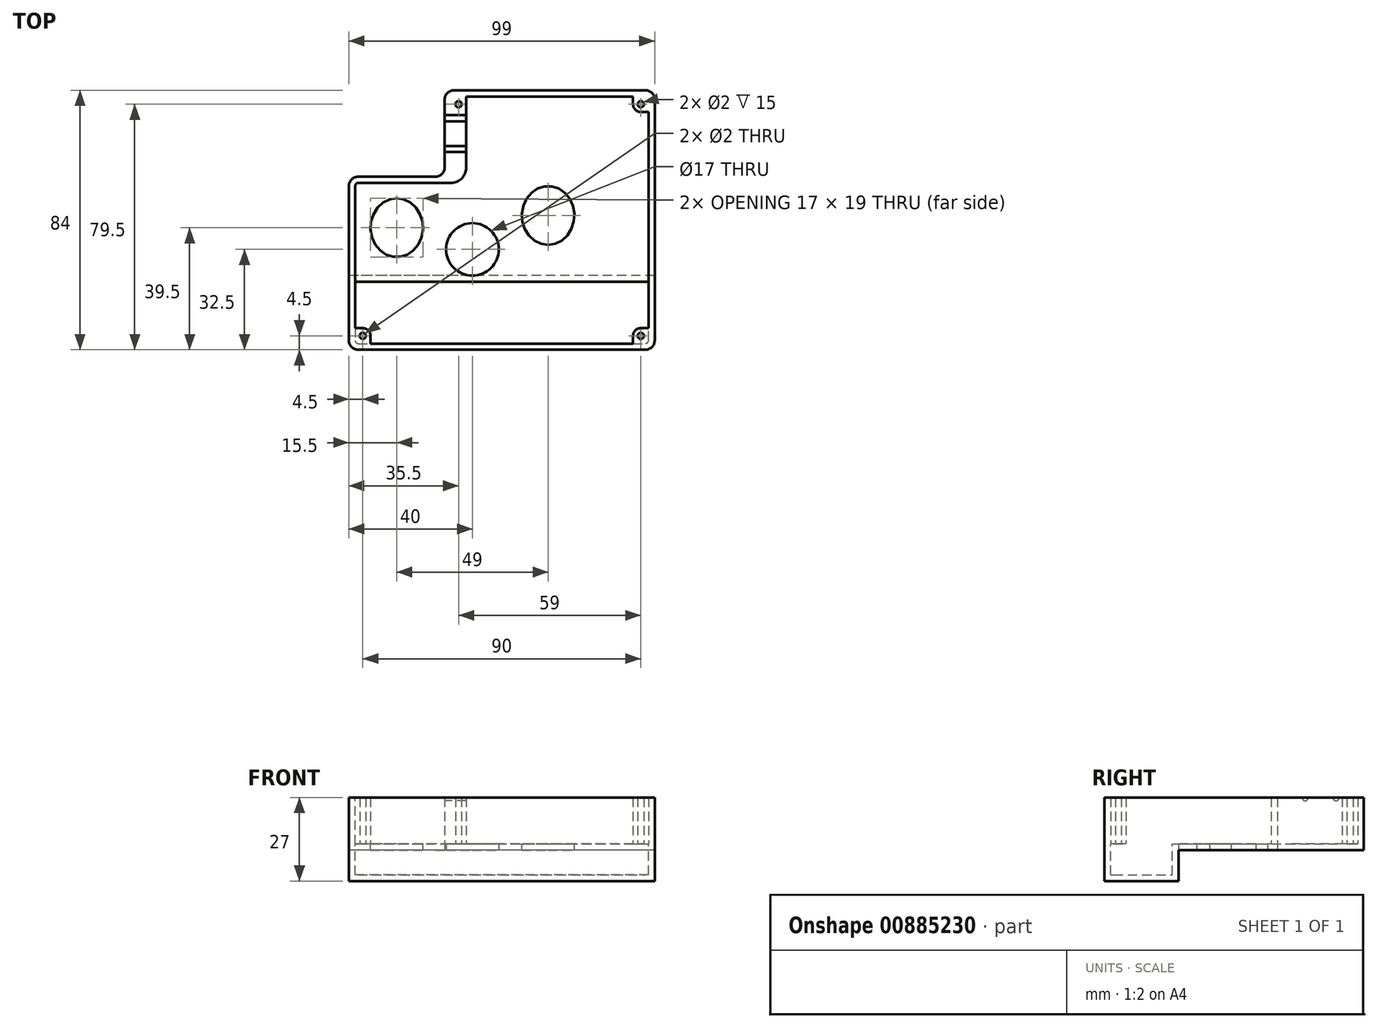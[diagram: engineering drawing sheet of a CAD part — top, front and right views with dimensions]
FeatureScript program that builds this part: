
annotation { "Feature Type Name" : "Feature", "Feature Type Description" : "" }
export const myFeature = defineFeature(function(context is Context, id is Id, definition is map)
    precondition{}
    {
        {
            var Q0;
            Q0=qCreatedBy(makeId("Top.planeOp"),FACE);
            var sketch = newSketch(context, id + "F0", { "sketchPlane" : qUnion([Q0])});
            skPoint(sketch, "E0.middle", {"position": v(0, 0) * mm});
            skPoint(sketch, "E1.visualSharp", {"position": v(-40.5, 17.5) * mm});
            skArc(sketch, "E1.filletArc", {"start": v(-37.5, 17.5) * mm, "mid": v(-39.62, 16.62) * mm, "end": v(-40.5, 14.5) * mm});
            skPoint(sketch, "E2.visualSharp", {"position": v(40.5, 17.5) * mm});
            skLineSegment(sketch, "E3", {"start": v(40.5, 17.5) * mm, "end": v(40.5, 42.5) * mm});
            skLineSegment(sketch, "E4", {"start": v(37.5, 45.5) * mm, "end": v(-6.5, 45.5) * mm});
            skLineSegment(sketch, "E5", {"start": v(-9.5, 42.5) * mm, "end": v(-9.5, 20.5) * mm});
            skLineSegment(sketch, "E6", {"start": v(-12.5, 17.5) * mm, "end": v(-37.5, 17.5) * mm});
            skPoint(sketch, "E7.visualSharp", {"position": v(-9.5, 17.5) * mm});
            skArc(sketch, "E7.filletArc", {"start": v(-12.5, 17.5) * mm, "mid": v(-10.38, 18.38) * mm, "end": v(-9.5, 20.5) * mm});
            skPoint(sketch, "E8.visualSharp", {"position": v(-9.5, 45.5) * mm});
            skArc(sketch, "E8.filletArc", {"start": v(-6.5, 45.5) * mm, "mid": v(-8.62, 44.62) * mm, "end": v(-9.5, 42.5) * mm});
            skPoint(sketch, "E9.visualSharp", {"position": v(40.5, 45.5) * mm});
            skArc(sketch, "E9.filletArc", {"start": v(40.5, 42.5) * mm, "mid": v(39.62, 44.62) * mm, "end": v(37.5, 45.5) * mm});
            skLineSegment(sketch, "E10", {"start": v(40.5, 17.5) * mm, "end": v(40.5, -17.5) * mm});
            skLineSegment(sketch, "E11", {"start": v(-40.5, -17.5) * mm, "end": v(-40.5, 14.5) * mm});
            skLineSegment(sketch, "E12", {"start": v(-40.5, -17.5) * mm, "end": v(-40.5, -17.5) * mm});
            skLineSegment(sketch, "E13", {"start": v(-40.5, -17.5) * mm, "end": v(-40.5, -35.5) * mm});
            skLineSegment(sketch, "E14", {"start": v(-37.5, -38.5) * mm, "end": v(55.5, -38.5) * mm});
            skLineSegment(sketch, "E15", {"start": v(58.5, -35.5) * mm, "end": v(58.5, -17.5) * mm});
            skLineSegment(sketch, "E16", {"start": v(58.5, -17.5) * mm, "end": v(40.5, -17.5) * mm});
            skLineSegment(sketch, "E17", {"start": v(58.5, -17.5) * mm, "end": v(58.5, 42.5) * mm});
            skLineSegment(sketch, "E18", {"start": v(55.5, 45.5) * mm, "end": v(37.5, 45.5) * mm});
            skPoint(sketch, "E19.visualSharp", {"position": v(58.5, -38.5) * mm});
            skArc(sketch, "E19.filletArc", {"start": v(55.5, -38.5) * mm, "mid": v(57.62, -37.62) * mm, "end": v(58.5, -35.5) * mm});
            skPoint(sketch, "E20.visualSharp", {"position": v(-40.5, -38.5) * mm});
            skArc(sketch, "E20.filletArc", {"start": v(-40.5, -35.5) * mm, "mid": v(-39.62, -37.62) * mm, "end": v(-37.5, -38.5) * mm});
            skPoint(sketch, "E21.visualSharp", {"position": v(58.5, 45.5) * mm});
            skArc(sketch, "E21.filletArc", {"start": v(58.5, 42.5) * mm, "mid": v(57.62, 44.62) * mm, "end": v(55.5, 45.5) * mm});
            skSolve(sketch);
        }
        {
            var Q0;
            Q0 = qSketchRegion(id + "F0", true);
            extrude(context, id + "F1", {"entities" : qUnion([Q0]), "depth" : 17 * mm, "offsetDistance" : 25 * mm});
        }
        {
            var Q0;
            Q0=qCreatedBy(makeId("Top.planeOp"),FACE);
            var sketch = newSketch(context, id + "F2", { "sketchPlane" : qUnion([Q0])});
            skEllipse(sketch, "E22", {"center": v(-25, 1) * mm, "majorRadius": 9.5 * mm, "minorRadius": 8.5 * mm, "majorAxis": v(0, 1)});
            skEllipse(sketch, "E23.MirrorC", {"center": v(24, 5) * mm, "majorRadius": 9.5 * mm, "minorRadius": 8.5 * mm, "majorAxis": v(0, -1)});
            skCircle(sketch, "E24", {"center": v(-0.5, -6) * mm, "radius": 8.5 * mm});
            skSolve(sketch);
        }
        {
            var Q0;
            Q0=makeQuery(id+"F1.opExtrude","CAP_FACE",FACE,{"disambiguationData":[OSD([sQuery(id+"F0.wireOp",EDGE,"E0.bottom"),sQuery(id+"F0.wireOp",EDGE,"E0.top"),sQuery(id+"F0.wireOp",EDGE,"E0.left"),sQuery(id+"F0.wireOp",EDGE,"E0.right"),sQuery(id+"F0.wireOp",EDGE,"E1.filletArc"),sQuery(id+"F0.wireOp",EDGE,"E2.filletArc"),sQuery(id+"F0.wireOp",EDGE,"fd3a0fd0-5bb6-43b4-b1ca-f7e2fdb911ee.filletArc"),sQuery(id+"F0.wireOp",EDGE,"6f945ab3-a14b-4210-82b2-7dc400fba289.filletArc"),sQuery(id+"F0.wireOp",EDGE,"lKBWg51h-oEnW-cZ2k-sGJy-vkzMBgg1EJc2")])],"isStart":false});
            shell(context, id + "F3", {"entities" : qUnion([Q0]), "thickness" : 2 * mm});
        }
        {
            var Q0;
            Q0 = qSketchRegion(id + "F2", true);
            extrude(context, id + "F4", {"entities" : qUnion([Q0]), "operationType" : NewBodyOperationType.REMOVE, "endBound" : BoundingType.UP_TO_NEXT, "depth" : 25 * mm, "offsetDistance" : 25 * mm});
        }
        {
            var Q0;
            Q0=makeQuery(id+"F3.opShell","OFFSET_FACE",FACE,{"disambiguationData":[OSD([sQuery(id+"F0.wireOp",EDGE,"E1.filletArc"),sQuery(id+"F0.wireOp",EDGE,"E4"),sQuery(id+"F0.wireOp",EDGE,"E5"),sQuery(id+"F0.wireOp",EDGE,"E6"),sQuery(id+"F0.wireOp",EDGE,"E7.filletArc"),sQuery(id+"F0.wireOp",EDGE,"E8.filletArc"),sQuery(id+"F0.wireOp",EDGE,"E11"),sQuery(id+"F0.wireOp",EDGE,"E13"),sQuery(id+"F0.wireOp",EDGE,"E14"),sQuery(id+"F0.wireOp",EDGE,"E15"),sQuery(id+"F0.wireOp",EDGE,"E17"),sQuery(id+"F0.wireOp",EDGE,"E18"),sQuery(id+"F0.wireOp",EDGE,"E19.filletArc"),sQuery(id+"F0.wireOp",EDGE,"E20.filletArc"),sQuery(id+"F0.wireOp",EDGE,"E21.filletArc")])]});
            var sketch = newSketch(context, id + "F5", { "sketchPlane" : qUnion([Q0])});
            skCircle(sketch, "E25.0", {"center": v(54, 41) * mm, "radius": 1 * mm});
            skLineSegment(sketch, "E26", {"start": v(54, 38.5) * mm, "end": v(56.5, 38.5) * mm});
            skLineSegment(sketch, "E27", {"start": v(51.5, 41) * mm, "end": v(51.5, 43.5) * mm});
            skArc(sketch, "E28", {"start": v(51.5, 41) * mm, "mid": v(52.23, 39.23) * mm, "end": v(54, 38.5) * mm});
            skLineSegment(sketch, "E29", {"start": v(56.5, 38.5) * mm, "end": v(56.5, 43.5) * mm});
            skLineSegment(sketch, "E30", {"start": v(56.5, 43.5) * mm, "end": v(51.5, 43.5) * mm});
            skLineSegment(sketch, "E31", {"start": v(24.5, 43.5) * mm, "end": v(24.5, 26.84) * mm, "construction": true});
            skLineSegment(sketch, "E32.MirrorCS", {"start": v(-7.5, 43.5) * mm, "end": v(-2.5, 43.5) * mm});
            skLineSegment(sketch, "E33.MirrorCS", {"start": v(-7.5, 38.5) * mm, "end": v(-7.5, 43.5) * mm});
            skCircle(sketch, "E34.MirrorC", {"center": v(-5, 41) * mm, "radius": 1 * mm});
            skLineSegment(sketch, "E35", {"start": v(56.5, 3.5) * mm, "end": v(42, 3.5) * mm, "construction": true});
            skLineSegment(sketch, "E36.MirrorCS", {"start": v(54, -31.5) * mm, "end": v(56.5, -31.5) * mm});
            skArc(sketch, "E37.MirrorCS", {"start": v(51.5, -34) * mm, "mid": v(52.23, -32.23) * mm, "end": v(54, -31.5) * mm});
            skLineSegment(sketch, "E38.MirrorCS", {"start": v(51.5, -34) * mm, "end": v(51.5, -36.5) * mm});
            skLineSegment(sketch, "E39.MirrorCS", {"start": v(56.5, -31.5) * mm, "end": v(56.5, -36.5) * mm});
            skLineSegment(sketch, "E40.MirrorCS", {"start": v(56.5, -36.5) * mm, "end": v(51.5, -36.5) * mm});
            skCircle(sketch, "E41.MirrorC", {"center": v(54, -34) * mm, "radius": 1 * mm});
            skLineSegment(sketch, "E42", {"start": v(9, -36.5) * mm, "end": v(9, -20.27) * mm, "construction": true});
            skLineSegment(sketch, "E43.MirrorCS", {"start": v(-33.5, -34) * mm, "end": v(-33.5, -36.5) * mm});
            skArc(sketch, "E44.MirrorCS", {"start": v(-33.5, -34) * mm, "mid": v(-34.23, -32.23) * mm, "end": v(-36, -31.5) * mm});
            skLineSegment(sketch, "E45.MirrorCS", {"start": v(-36, -31.5) * mm, "end": v(-38.5, -31.5) * mm});
            skCircle(sketch, "E46.MirrorC", {"center": v(-36, -34) * mm, "radius": 1 * mm});
            skLineSegment(sketch, "E47.MirrorCS", {"start": v(-38.5, -36.5) * mm, "end": v(-33.5, -36.5) * mm});
            skLineSegment(sketch, "E48.MirrorCS", {"start": v(-38.5, -31.5) * mm, "end": v(-38.5, -36.5) * mm});
            skLineSegment(sketch, "E49", {"start": v(-2.5, 43.5) * mm, "end": v(-2.5, 20.5) * mm});
            skLineSegment(sketch, "E50", {"start": v(-7.5, 15.5) * mm, "end": v(-12.5, 15.5) * mm});
            skLineSegment(sketch, "E51", {"start": v(-12.5, 15.5) * mm, "end": v(-7.5, 20.5) * mm});
            skLineSegment(sketch, "E52", {"start": v(-7.5, 20.5) * mm, "end": v(-7.5, 38.5) * mm});
            skPoint(sketch, "E53.visualSharp", {"position": v(-2.5, 15.5) * mm});
            skArc(sketch, "E53.filletArc", {"start": v(-7.5, 15.5) * mm, "mid": v(-3.96, 16.96) * mm, "end": v(-2.5, 20.5) * mm});
            skSolve(sketch);
        }
        {
            var Q0;
            Q0 = qSketchRegion(id + "F5", true);
            var Q1;
            {var subQ0=sQuery(id+"F0.wireOp",EDGE,"E19.filletArc");var subQ1=sQuery(id+"F0.wireOp",EDGE,"E17");var subQ2=sQuery(id+"F0.wireOp",EDGE,"E15");var subQ3=sQuery(id+"F0.wireOp",EDGE,"E21.filletArc");var subQ4=sQuery(id+"F0.wireOp",EDGE,"E14");var subQ5=sQuery(id+"F0.wireOp",EDGE,"E20.filletArc");var subQ6=sQuery(id+"F0.wireOp",EDGE,"E1.filletArc");var subQ7=sQuery(id+"F0.wireOp",EDGE,"E5");var subQ8=sQuery(id+"F0.wireOp",EDGE,"E18");var subQ9=sQuery(id+"F0.wireOp",EDGE,"E4");var subQ10=sQuery(id+"F0.wireOp",EDGE,"E6");var subQ11=sQuery(id+"F0.wireOp",EDGE,"E13");var subQ12=sQuery(id+"F0.wireOp",EDGE,"E11");var subQ13=sQuery(id+"F0.wireOp",EDGE,"E7.filletArc");var subQ14=sQuery(id+"F0.wireOp",EDGE,"E8.filletArc");Q1=makeQuery(id+"F8.boolean.opBoolean","SPLIT",FACE,{"disambiguationData":[TD([makeQuery(id+"F1.opExtrude","SWEPT_FACE",FACE,{"disambiguationData":[OSD([subQ6])]}),makeQuery(id+"F1.opExtrude","SWEPT_FACE",FACE,{"disambiguationData":[OSD([subQ9,subQ8])]}),makeQuery(id+"F1.opExtrude","SWEPT_FACE",FACE,{"disambiguationData":[OSD([subQ7])]}),makeQuery(id+"F1.opExtrude","SWEPT_FACE",FACE,{"disambiguationData":[OSD([subQ10])]}),makeQuery(id+"F1.opExtrude","SWEPT_FACE",FACE,{"disambiguationData":[OSD([subQ13])]}),makeQuery(id+"F1.opExtrude","SWEPT_FACE",FACE,{"disambiguationData":[OSD([subQ14])]}),makeQuery(id+"F1.opExtrude","SWEPT_FACE",FACE,{"disambiguationData":[OSD([subQ12,subQ11])]}),makeQuery(id+"F1.opExtrude","SWEPT_FACE",FACE,{"disambiguationData":[OSD([subQ4])]}),makeQuery(id+"F1.opExtrude","SWEPT_FACE",FACE,{"disambiguationData":[OSD([subQ2,subQ1])]}),makeQuery(id+"F1.opExtrude","SWEPT_FACE",FACE,{"disambiguationData":[OSD([subQ0])]}),makeQuery(id+"F1.opExtrude","SWEPT_FACE",FACE,{"disambiguationData":[OSD([subQ5])]}),makeQuery(id+"F1.opExtrude","SWEPT_FACE",FACE,{"disambiguationData":[OSD([subQ3])]}),makeQuery(id+"F3.opShell","OFFSET_FACE",FACE,{"disambiguationData":[OSD([subQ6])]}),makeQuery(id+"F3.opShell","OFFSET_FACE",FACE,{"disambiguationData":[OSD([subQ9,subQ8])]}),makeQuery(id+"F3.opShell","OFFSET_FACE",FACE,{"disambiguationData":[OSD([subQ7])]}),makeQuery(id+"F3.opShell","OFFSET_FACE",FACE,{"disambiguationData":[OSD([subQ10])]}),makeQuery(id+"F3.opShell","OFFSET_FACE",FACE,{"disambiguationData":[OSD([subQ13])]}),makeQuery(id+"F3.opShell","OFFSET_FACE",FACE,{"disambiguationData":[OSD([subQ14])]}),makeQuery(id+"F3.opShell","OFFSET_FACE",FACE,{"disambiguationData":[OSD([subQ12,subQ11])]}),makeQuery(id+"F3.opShell","OFFSET_FACE",FACE,{"disambiguationData":[OSD([subQ4])]}),makeQuery(id+"F3.opShell","OFFSET_FACE",FACE,{"disambiguationData":[OSD([subQ2,subQ1])]}),makeQuery(id+"F3.opShell","OFFSET_FACE",FACE,{"disambiguationData":[OSD([subQ0])]}),makeQuery(id+"F3.opShell","OFFSET_FACE",FACE,{"disambiguationData":[OSD([subQ5])]}),makeQuery(id+"F3.opShell","OFFSET_FACE",FACE,{"disambiguationData":[OSD([subQ3])]}),makeQuery(id+"F8.opExtrude","SWEPT_FACE",FACE,{"disambiguationData":[OSD([sQuery(id+"F7.wireOp",EDGE,"E54")])]}),makeQuery(id+"F8.opExtrude","SWEPT_FACE",FACE,{"disambiguationData":[OSD([sQuery(id+"F7.wireOp",EDGE,"E55")])]})])],"derivedFrom":makeQuery(id+"F1.opExtrude","CAP_FACE",FACE,{"disambiguationData":[OSD([subQ6,subQ9,subQ7,subQ10,subQ13,subQ14,subQ12,subQ11,subQ4,subQ2,subQ1,subQ8,subQ0,subQ5,subQ3])],"isStart":false})});}
            extrude(context, id + "F6", {"entities" : qUnion([Q0]), "operationType" : NewBodyOperationType.ADD, "endBound" : BoundingType.UP_TO_SURFACE, "depth" : 25 * mm, "endBoundEntityFace" : qUnion([Q1]), "offsetDistance" : 25 * mm});
        }
        {
            var Q0;
            Q0=makeQuery(id+"F1.opExtrude","SWEPT_FACE",FACE,{"disambiguationData":[OSD([sQuery(id+"F0.wireOp",EDGE,"E5")])]});
            var sketch = newSketch(context, id + "F7", { "sketchPlane" : qUnion([Q0])});
            skCircle(sketch, "E54", {"center": v(-26.5, 17) * mm, "radius": 1 * mm});
            skCircle(sketch, "E55", {"center": v(-36.5, 17) * mm, "radius": 1 * mm});
            skSolve(sketch);
        }
        {
            var Q0;
            Q0 = qSketchRegion(id + "F7", true);
            extrude(context, id + "F8", {"entities" : qUnion([Q0]), "operationType" : NewBodyOperationType.REMOVE, "endBound" : BoundingType.UP_TO_NEXT, "oppositeDirection" : true, "depth" : 25 * mm, "offsetDistance" : 25 * mm});
        }
        {
            var Q0;
            Q0=makeQuery(id+"F1.opExtrude","CAP_FACE",FACE,{"disambiguationData":[OSD([sQuery(id+"F0.wireOp",EDGE,"E1.filletArc"),sQuery(id+"F0.wireOp",EDGE,"E4"),sQuery(id+"F0.wireOp",EDGE,"E5"),sQuery(id+"F0.wireOp",EDGE,"E6"),sQuery(id+"F0.wireOp",EDGE,"E7.filletArc"),sQuery(id+"F0.wireOp",EDGE,"E8.filletArc"),sQuery(id+"F0.wireOp",EDGE,"E11"),sQuery(id+"F0.wireOp",EDGE,"E13"),sQuery(id+"F0.wireOp",EDGE,"E14"),sQuery(id+"F0.wireOp",EDGE,"E15"),sQuery(id+"F0.wireOp",EDGE,"E17"),sQuery(id+"F0.wireOp",EDGE,"E18"),sQuery(id+"F0.wireOp",EDGE,"E19.filletArc"),sQuery(id+"F0.wireOp",EDGE,"E20.filletArc"),sQuery(id+"F0.wireOp",EDGE,"E21.filletArc")])],"isStart":true});
            var sketch = newSketch(context, id + "F9", { "sketchPlane" : qUnion([Q0])});
            skLineSegment(sketch, "E56.0", {"start": v(-37.5, 38.5) * mm, "end": v(55.5, 38.5) * mm, "construction": true});
            skArc(sketch, "E57.0", {"start": v(-40.5, 35.5) * mm, "mid": v(-39.62, 37.62) * mm, "end": v(-37.5, 38.5) * mm, "construction": true});
            skArc(sketch, "E57.1", {"start": v(55.5, 38.5) * mm, "mid": v(57.62, 37.62) * mm, "end": v(58.5, 35.5) * mm, "construction": true});
            skLineSegment(sketch, "E58", {"start": v(58.5, 35.5) * mm, "end": v(58.5, 14.5) * mm, "construction": true});
            skLineSegment(sketch, "E59", {"start": v(58.5, 14.5) * mm, "end": v(-40.5, 14.5) * mm, "construction": true});
            skLineSegment(sketch, "E60", {"start": v(-40.5, 14.5) * mm, "end": v(-40.5, 35.5) * mm, "construction": true});
            skLineSegment(sketch, "E61.0", {"start": v(56.5, 35.5) * mm, "end": v(56.5, 16.5) * mm});
            skLineSegment(sketch, "E61.1", {"start": v(-38.5, 16.5) * mm, "end": v(-38.5, 35.5) * mm});
            skArc(sketch, "E61.2", {"start": v(-38.5, 35.5) * mm, "mid": v(-38.2, 36.2) * mm, "end": v(-37.5, 36.5) * mm});
            skLineSegment(sketch, "E61.3", {"start": v(56.5, 16.5) * mm, "end": v(-38.5, 16.5) * mm});
            skLineSegment(sketch, "E61.4", {"start": v(-37.5, 36.5) * mm, "end": v(55.5, 36.5) * mm});
            skArc(sketch, "E61.5", {"start": v(55.5, 36.5) * mm, "mid": v(56.2, 36.2) * mm, "end": v(56.5, 35.5) * mm});
            skSolve(sketch);
        }
        {
            var Q0;
            Q0=makeQuery(id+"F1.opExtrude","CAP_FACE",FACE,{"disambiguationData":[OSD([sQuery(id+"F0.wireOp",EDGE,"E1.filletArc"),sQuery(id+"F0.wireOp",EDGE,"E4"),sQuery(id+"F0.wireOp",EDGE,"E5"),sQuery(id+"F0.wireOp",EDGE,"E6"),sQuery(id+"F0.wireOp",EDGE,"E7.filletArc"),sQuery(id+"F0.wireOp",EDGE,"E8.filletArc"),sQuery(id+"F0.wireOp",EDGE,"E11"),sQuery(id+"F0.wireOp",EDGE,"E13"),sQuery(id+"F0.wireOp",EDGE,"E14"),sQuery(id+"F0.wireOp",EDGE,"E15"),sQuery(id+"F0.wireOp",EDGE,"E17"),sQuery(id+"F0.wireOp",EDGE,"E18"),sQuery(id+"F0.wireOp",EDGE,"E19.filletArc"),sQuery(id+"F0.wireOp",EDGE,"E20.filletArc"),sQuery(id+"F0.wireOp",EDGE,"E21.filletArc")])],"isStart":true});
            var sketch = newSketch(context, id + "F10", { "sketchPlane" : qUnion([Q0])});
            skLineSegment(sketch, "E62.0", {"start": v(-37.5, 38.5) * mm, "end": v(55.5, 38.5) * mm});
            skArc(sketch, "E63.0", {"start": v(-40.5, 35.5) * mm, "mid": v(-39.62, 37.62) * mm, "end": v(-37.5, 38.5) * mm});
            skArc(sketch, "E64.0", {"start": v(55.5, 38.5) * mm, "mid": v(57.62, 37.62) * mm, "end": v(58.5, 35.5) * mm});
            skLineSegment(sketch, "E65", {"start": v(58.5, 35.5) * mm, "end": v(58.5, 14.5) * mm});
            skLineSegment(sketch, "E66", {"start": v(58.5, 14.5) * mm, "end": v(-40.5, 14.5) * mm});
            skPoint(sketch, "E66.endSnap0", {"position": v(-40.5, 10.5) * mm});
            skLineSegment(sketch, "E67", {"start": v(-40.5, 14.5) * mm, "end": v(-40.5, 35.5) * mm});
            skSolve(sketch);
        }
        {
            var Q0;
            Q0=makeQuery(id+"F10.imprint","IMPRINT",FACE,{"disambiguationData":[TD([[makeQuery(id+"F10.imprint","IMPRINT",EDGE,{"derivedFrom":sQuery(id+"F10.wireOp",EDGE,"E62.0")}),-1.0]])]});
            extrude(context, id + "F11", {"entities" : qUnion([Q0]), "operationType" : NewBodyOperationType.ADD, "depth" : 10 * mm, "offsetDistance" : 25 * mm});
        }
        {
            var Q0;
            Q0 = qSketchRegion(id + "F9", true);
            var Q1;
            Q1 = qConstructionFilter(qBodyType(qCreatedBy(id + "F9" ,EDGE), BodyType.WIRE), ConstructionObject.NO);
            extrude(context, id + "F12", {"entities" : qUnion([Q0]), "operationType" : NewBodyOperationType.REMOVE, "surfaceEntities" : qUnion([Q1]), "depth" : 8 * mm, "offsetDistance" : 25 * mm});
        }
        {
            var Q0;
            Q0 = qSketchRegion(id + "F9", true);
            extrude(context, id + "F13", {"entities" : qUnion([Q0]), "operationType" : NewBodyOperationType.REMOVE, "oppositeDirection" : true, "depth" : 2 * mm, "offsetDistance" : 25 * mm});
        }
    });
